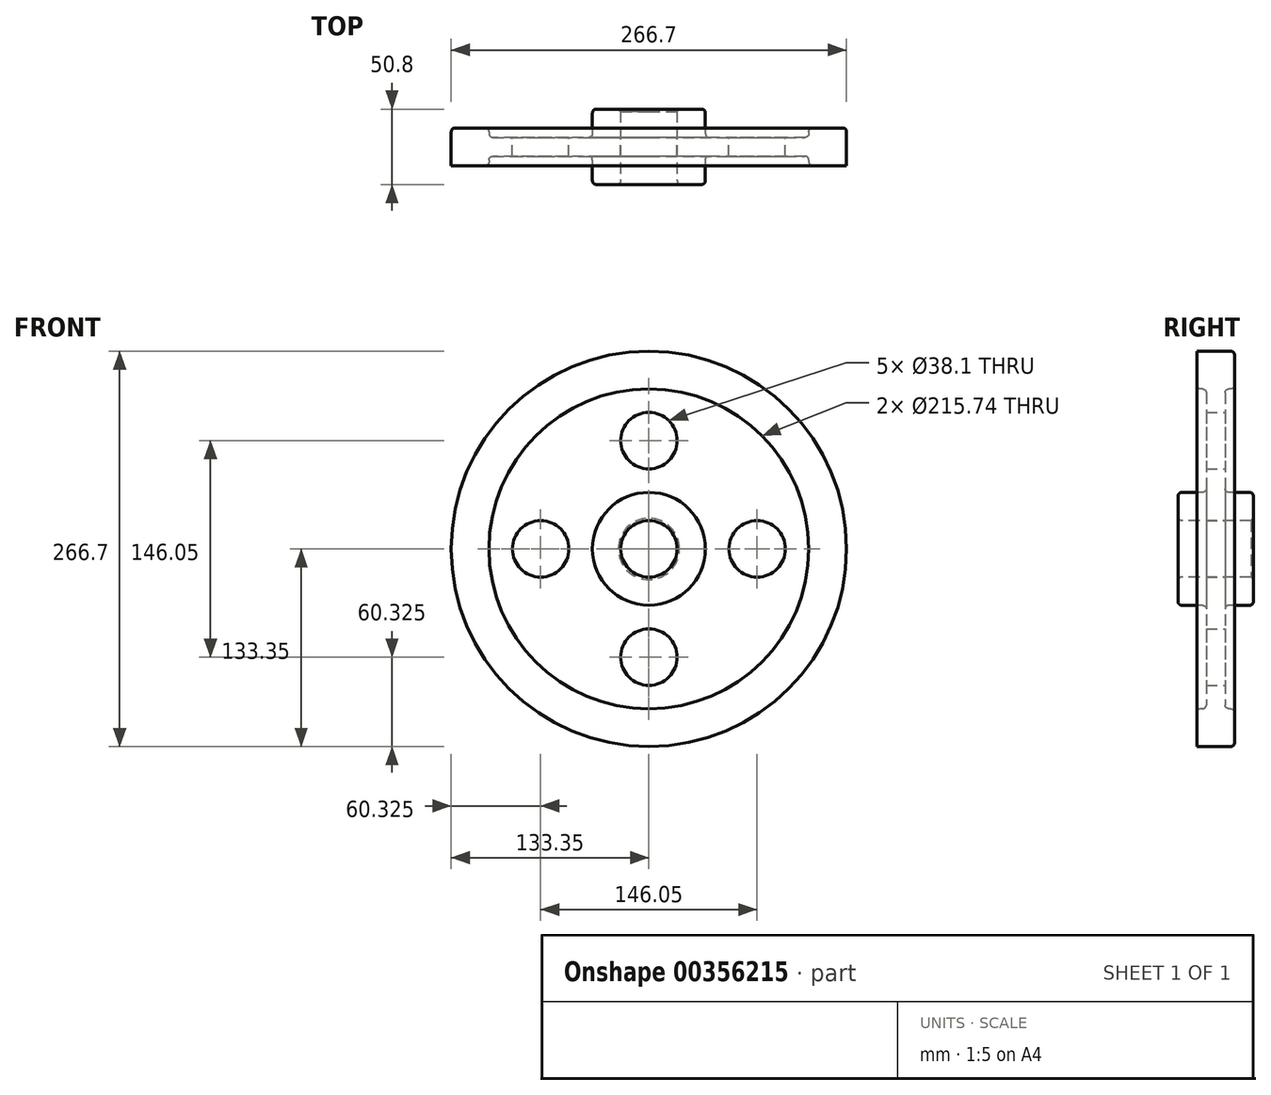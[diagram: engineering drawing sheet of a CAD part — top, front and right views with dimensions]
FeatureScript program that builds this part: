
annotation { "Feature Type Name" : "Feature", "Feature Type Description" : "" }
export const myFeature = defineFeature(function(context is Context, id is Id, definition is map)
    precondition{}
    {
        {
            var Q0;
            Q0=qCreatedBy(makeId("Right.planeOp"),FACE);
            var sketch = newSketch(context, id + "F0", { "sketchPlane" : qUnion([Q0])});
            skLineSegment(sketch, "E0", {"start": v(0, 0) * mm, "end": v(74.98, 0) * mm, "construction": true});
            skLineSegment(sketch, "E1.0", {"start": v(12.7, 19.05) * mm, "end": v(25.4, 19.05) * mm});
            skLineSegment(sketch, "E2.0", {"start": v(6.35, 38.1) * mm, "end": v(25.4, 38.1) * mm});
            skLineSegment(sketch, "E3.0", {"start": v(0, 133.35) * mm, "end": v(12.7, 133.35) * mm});
            skLineSegment(sketch, "E4", {"start": v(0, 133.35) * mm, "end": v(0, 19.05) * mm});
            skLineSegment(sketch, "E5.0", {"start": v(25.4, 38.1) * mm, "end": v(25.4, 19.05) * mm});
            skLineSegment(sketch, "E6.0", {"start": v(12.7, 133.35) * mm, "end": v(12.7, 107.87) * mm});
            skLineSegment(sketch, "E7", {"start": v(0, 19.05) * mm, "end": v(12.7, 19.05) * mm});
            skLineSegment(sketch, "E8", {"start": v(6.35, 107.87) * mm, "end": v(12.7, 107.87) * mm});
            skLineSegment(sketch, "E9", {"start": v(6.35, 107.87) * mm, "end": v(6.35, 38.1) * mm});
            skPoint(sketch, "E10.0.end.orphan", {"position": v(6.35, 19.05) * mm});
            skLineSegment(sketch, "E11.MirrorCS", {"start": v(-12.7, 133.35) * mm, "end": v(-12.7, 107.87) * mm});
            skLineSegment(sketch, "E12.MirrorCS", {"start": v(-6.35, 107.87) * mm, "end": v(-6.35, 38.1) * mm});
            skLineSegment(sketch, "E13.MirrorCS", {"start": v(-6.35, 38.1) * mm, "end": v(-25.4, 38.1) * mm});
            skLineSegment(sketch, "E14.MirrorCS", {"start": v(-12.7, 19.05) * mm, "end": v(-25.4, 19.05) * mm});
            skLineSegment(sketch, "E15.MirrorCS", {"start": v(-25.4, 38.1) * mm, "end": v(-25.4, 19.05) * mm});
            skLineSegment(sketch, "E16.MirrorCS", {"start": v(0, 133.35) * mm, "end": v(-12.7, 133.35) * mm});
            skLineSegment(sketch, "E17", {"start": v(-12.7, 107.87) * mm, "end": v(12.7, 107.87) * mm});
            skLineSegment(sketch, "E18", {"start": v(-12.7, 19.05) * mm, "end": v(12.7, 19.05) * mm});
            skSolve(sketch);
        }
        {
            var Q0;
            {var subQ1=sQuery(id+"F0.wireOp",EDGE,"E12.MirrorCS");Q0=makeQuery(id+"F0.imprint","IMPRINT",FACE,{"disambiguationData":[TD([[makeQuery(id+"F0.imprint","IMPRINT",EDGE,{"derivedFrom":subQ1}),1.0]])]});}
            var Q1;
            {var subQ6=sQuery(id+"F0.wireOp",EDGE,"E1.0");Q1=makeQuery(id+"F0.imprint","IMPRINT",FACE,{"disambiguationData":[TD([[makeQuery(id+"F0.imprint","IMPRINT",EDGE,{"derivedFrom":subQ6}),1.0]])]});}
            var Q2;
            {var subQ3=sQuery(id+"F0.wireOp",EDGE,"E16.MirrorCS");Q2=makeQuery(id+"F0.imprint","IMPRINT",FACE,{"disambiguationData":[TD([[makeQuery(id+"F0.imprint","IMPRINT",EDGE,{"derivedFrom":subQ3}),1.0]])]});}
            var Q3;
            {var subQ5=sQuery(id+"F0.wireOp",EDGE,"E3.0");Q3=makeQuery(id+"F0.imprint","IMPRINT",FACE,{"disambiguationData":[TD([[makeQuery(id+"F0.imprint","IMPRINT",EDGE,{"derivedFrom":subQ5}),-1.0]])]});}
            var Q4;
            Q4=sQuery(id+"F0.wireOp",EDGE,"E0");
            revolve(context, id + "F1", {"entities" : qUnion([Q0, Q1, Q2, Q3]), "axis" : qUnion([Q4]), "revolveType" : RevolveType.FULL});
        }
        {
            var Q0;
            Q0=makeQuery(id+"F1.opRevolve","SWEPT_FACE",FACE,{"disambiguationData":[OSD([sQuery(id+"F0.wireOp",EDGE,"E9")])]});
            var sketch = newSketch(context, id + "F2", { "sketchPlane" : qUnion([Q0])});
            skLineSegment(sketch, "E19", {"start": v(0, 0) * mm, "end": v(0, 73.03) * mm});
            skCircle(sketch, "E20", {"center": v(0, 73.03) * mm, "radius": 19.05 * mm});
            skCircle(sketch, "E21.1.0", {"center": v(-73.03, 0) * mm, "radius": 19.05 * mm});
            skCircle(sketch, "E21.2.0", {"center": v(0, -73.03) * mm, "radius": 19.05 * mm});
            skCircle(sketch, "E21.3.0", {"center": v(73.03, 0) * mm, "radius": 19.05 * mm});
            skPoint(sketch, "E21.center", {"position": v(0, 0) * mm});
            skSolve(sketch);
        }
        {
            var Q0;
            Q0=makeQuery(id+"F2.imprint","IMPRINT",FACE,{"disambiguationData":[TD([[makeQuery(id+"F2.imprint","IMPRINT",EDGE,{"derivedFrom":sQuery(id+"F2.wireOp",EDGE,"E21.1.0")}),1.0]])]});
            var Q1;
            Q1=makeQuery(id+"F2.imprint","IMPRINT",FACE,{"disambiguationData":[TD([[makeQuery(id+"F2.imprint","IMPRINT",EDGE,{"derivedFrom":sQuery(id+"F2.wireOp",EDGE,"E20")}),1.0]])]});
            var Q2;
            Q2=makeQuery(id+"F2.imprint","IMPRINT",FACE,{"disambiguationData":[TD([[makeQuery(id+"F2.imprint","IMPRINT",EDGE,{"derivedFrom":sQuery(id+"F2.wireOp",EDGE,"E21.3.0")}),1.0]])]});
            var Q3;
            Q3=makeQuery(id+"F2.imprint","IMPRINT",FACE,{"disambiguationData":[TD([[makeQuery(id+"F2.imprint","IMPRINT",EDGE,{"derivedFrom":sQuery(id+"F2.wireOp",EDGE,"E21.2.0")}),1.0]])]});
            extrude(context, id + "F3", {"entities" : qUnion([Q0, Q1, Q2, Q3]), "operationType" : NewBodyOperationType.REMOVE, "oppositeDirection" : true, "depth" : 25.4 * mm});
        }
        {
            var Q0;
            Q0=makeQuery(id+"F1.opRevolve","SWEPT_EDGE",EDGE,{"disambiguationData":[OSD([sQuery(id+"F0.wireOp",EDGE,"E9"),sQuery(id+"F0.wireOp",EDGE,"E17")])]});
            var Q1;
            Q1=makeQuery(id+"F1.opRevolve","SWEPT_EDGE",EDGE,{"disambiguationData":[OSD([sQuery(id+"F0.wireOp",EDGE,"E6.0"),sQuery(id+"F0.wireOp",EDGE,"E17")])]});
            var Q2;
            Q2=makeQuery(id+"F1.opRevolve","SWEPT_EDGE",EDGE,{"disambiguationData":[OSD([sQuery(id+"F0.wireOp",EDGE,"E2.0"),sQuery(id+"F0.wireOp",EDGE,"E5.0")])]});
            var Q3;
            Q3=makeQuery(id+"F1.opRevolve","SWEPT_EDGE",EDGE,{"disambiguationData":[OSD([sQuery(id+"F0.wireOp",EDGE,"E2.0"),sQuery(id+"F0.wireOp",EDGE,"E9")])]});
            var Q4;
            Q4=makeQuery(id+"F1.opRevolve","SWEPT_EDGE",EDGE,{"disambiguationData":[OSD([sQuery(id+"F0.wireOp",EDGE,"E12.MirrorCS"),sQuery(id+"F0.wireOp",EDGE,"E17")])]});
            var Q5;
            Q5=makeQuery(id+"F1.opRevolve","SWEPT_EDGE",EDGE,{"disambiguationData":[OSD([sQuery(id+"F0.wireOp",EDGE,"E11.MirrorCS"),sQuery(id+"F0.wireOp",EDGE,"E17")])]});
            var Q6;
            Q6=makeQuery(id+"F1.opRevolve","SWEPT_FACE",FACE,{"disambiguationData":[OSD([sQuery(id+"F0.wireOp",EDGE,"E15.MirrorCS")])]});
            var Q7;
            Q7=makeQuery(id+"F1.opRevolve","SWEPT_EDGE",EDGE,{"disambiguationData":[OSD([sQuery(id+"F0.wireOp",EDGE,"E12.MirrorCS"),sQuery(id+"F0.wireOp",EDGE,"E13.MirrorCS")])]});
            fillet(context, id + "F4", {"entities" : qUnion([Q0, Q1, Q2, Q3, Q4, Q5, Q6, Q7]), "radius" : 2.54 * mm, "tangentPropagation" : true, "allowEdgeOverflow" : false});
        }
        {
            var Q0;
            Q0=makeQuery(id+"F1.opRevolve","SWEPT_EDGE",EDGE,{"disambiguationData":[OSD([sQuery(id+"F0.wireOp",EDGE,"E1.0"),sQuery(id+"F0.wireOp",EDGE,"E5.0")])]});
            chamfer(context, id + "F5", {"entities" : qUnion([Q0]), "width" : 1.59 * mm, "tangentPropagation" : true});
        }
    });
